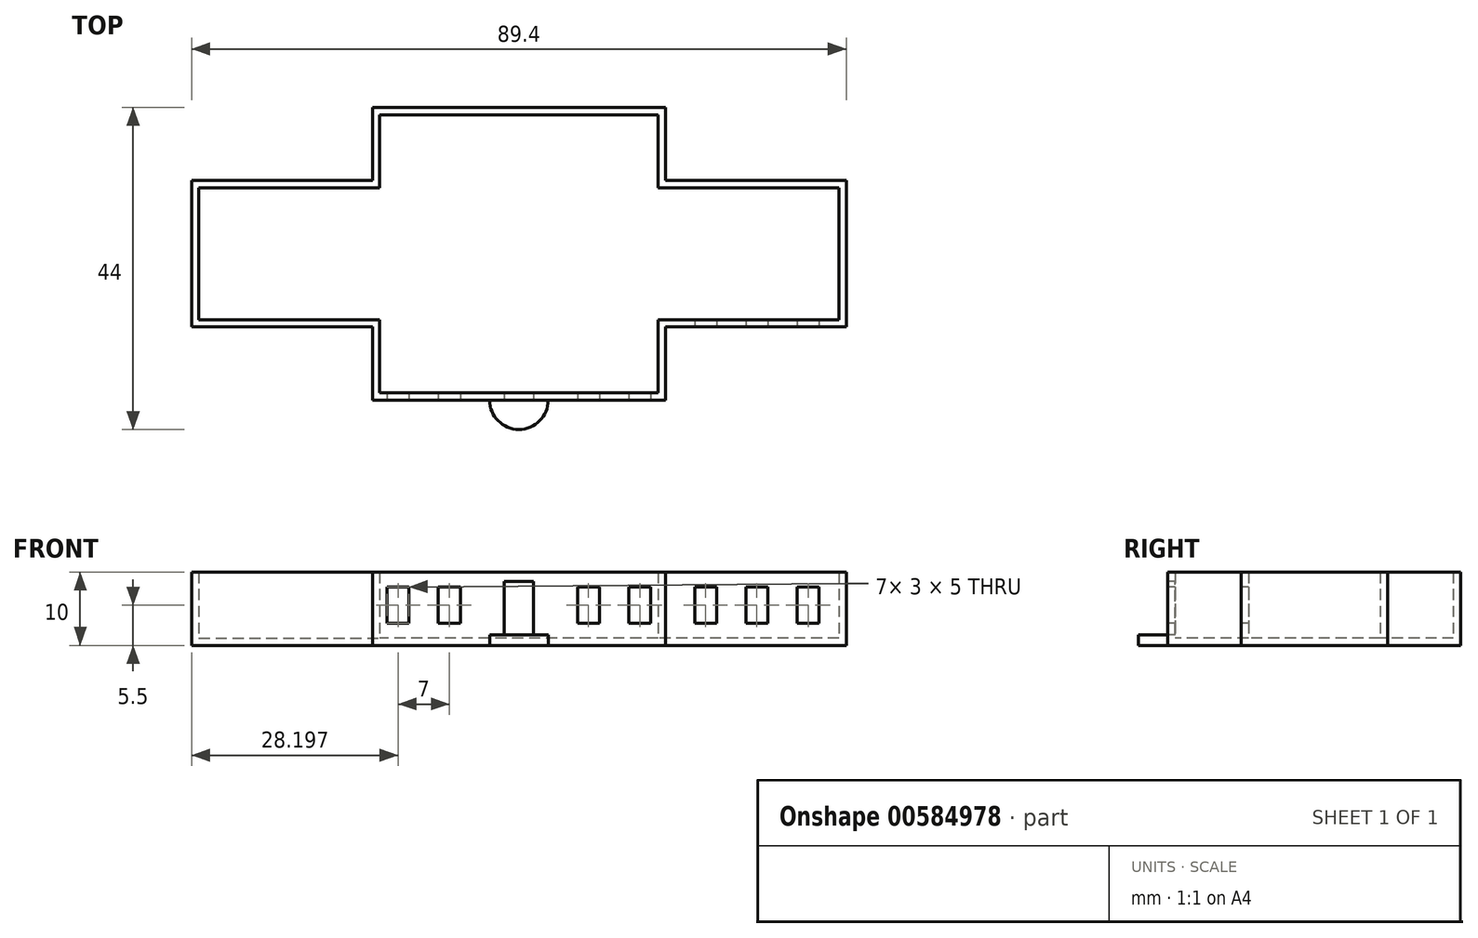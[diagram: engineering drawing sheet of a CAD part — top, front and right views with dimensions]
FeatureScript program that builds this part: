
annotation { "Feature Type Name" : "Feature", "Feature Type Description" : "" }
export const myFeature = defineFeature(function(context is Context, id is Id, definition is map)
    precondition{}
    {
        {
            var Q0;
            Q0=qCreatedBy(makeId("Top.planeOp"),FACE);
            var sketch = newSketch(context, id + "F0", { "sketchPlane" : qUnion([Q0])});
            skLineSegment(sketch, "E0", {"start": v(-44.66, 21.95) * mm, "end": v(-44.66, 31.95) * mm});
            skLineSegment(sketch, "E1", {"start": v(-44.66, 31.95) * mm, "end": v(-4.66, 31.95) * mm});
            skLineSegment(sketch, "E2", {"start": v(-4.66, 31.95) * mm, "end": v(-4.66, 21.95) * mm});
            skLineSegment(sketch, "E3", {"start": v(-4.66, 21.95) * mm, "end": v(20.04, 21.95) * mm});
            skLineSegment(sketch, "E4", {"start": v(20.04, 21.95) * mm, "end": v(20.04, 1.95) * mm});
            skLineSegment(sketch, "E5", {"start": v(20.04, 1.95) * mm, "end": v(-4.66, 1.95) * mm});
            skLineSegment(sketch, "E6", {"start": v(-4.66, 1.95) * mm, "end": v(-4.66, -8.05) * mm});
            skLineSegment(sketch, "E7", {"start": v(-4.66, -8.05) * mm, "end": v(-44.66, -8.05) * mm});
            skLineSegment(sketch, "E8", {"start": v(-44.66, -8.05) * mm, "end": v(-44.66, 1.95) * mm});
            skLineSegment(sketch, "E9", {"start": v(-44.66, 1.95) * mm, "end": v(-69.36, 1.95) * mm});
            skLineSegment(sketch, "E10", {"start": v(-69.36, 1.95) * mm, "end": v(-69.36, 21.95) * mm});
            skLineSegment(sketch, "E11", {"start": v(-69.36, 21.95) * mm, "end": v(-44.66, 21.95) * mm});
            skPoint(sketch, "E12", {"position": v(-24.66, -8.05) * mm});
            skCircle(sketch, "E13", {"center": v(-24.66, -8.05) * mm, "radius": 4 * mm});
            skPoint(sketch, "E14", {"position": v(-28.66, -8.05) * mm});
            skPoint(sketch, "E15", {"position": v(-20.66, -8.05) * mm});
            skSolve(sketch);
        }
        {
            var Q0;
            Q0=makeQuery(id+"F0.imprint","IMPRINT",FACE,{"disambiguationData":[TD([[makeQuery(id+"F0.imprint","IMPRINT",EDGE,{"derivedFrom":sQuery(id+"F0.wireOp",EDGE,"E0")}),-1.0]])]});
            var Q1;
            {var subQ0=sQuery(id+"F0.wireOp",EDGE,"E13");var subQ1=sQuery(id+"F0.wireOp",EDGE,"E7");var subQ2=makeQuery(id+"F0.imprint","INTERSECT",VERTEX,{"disambiguationData":[OD(0.0)],"derivedFrom":[subQ1,subQ0]});Q1=makeQuery(id+"F0.imprint","IMPRINT",FACE,{"disambiguationData":[TD([[makeQuery(id+"F0.imprint","IMPRINT",EDGE,{"disambiguationData":[TD([[subQ2,-1.0]])],"derivedFrom":subQ1}),-1.0]])]});}
            extrude(context, id + "F1", {"entities" : qUnion([Q0, Q1]), "depth" : 10 * mm, "offsetDistance" : 25 * mm});
        }
        {
            var Q0;
            Q0=makeQuery(id+"F1.opExtrude","CAP_FACE",FACE,{"disambiguationData":[OSD([sQuery(id+"F0.wireOp",EDGE,"E0"),sQuery(id+"F0.wireOp",EDGE,"E1"),sQuery(id+"F0.wireOp",EDGE,"E2"),sQuery(id+"F0.wireOp",EDGE,"E3"),sQuery(id+"F0.wireOp",EDGE,"E4"),sQuery(id+"F0.wireOp",EDGE,"E5"),sQuery(id+"F0.wireOp",EDGE,"E6"),sQuery(id+"F0.wireOp",EDGE,"E7"),sQuery(id+"F0.wireOp",EDGE,"E8"),sQuery(id+"F0.wireOp",EDGE,"E9"),sQuery(id+"F0.wireOp",EDGE,"E10"),sQuery(id+"F0.wireOp",EDGE,"E11")])],"isStart":false});
            shell(context, id + "F2", {"entities" : qUnion([Q0]), "thickness" : 1 * mm});
        }
        {
            var Q0;
            {var subQ0=sQuery(id+"F0.wireOp",EDGE,"E13");var subQ1=sQuery(id+"F0.wireOp",EDGE,"E7");var subQ2=makeQuery(id+"F0.imprint","INTERSECT",VERTEX,{"disambiguationData":[OD(0.0)],"derivedFrom":[subQ1,subQ0]});Q0=makeQuery(id+"F0.imprint","IMPRINT",FACE,{"disambiguationData":[TD([[makeQuery(id+"F0.imprint","IMPRINT",EDGE,{"disambiguationData":[TD([[subQ2,-1.0]])],"derivedFrom":subQ1}),1.0]])]});}
            extrude(context, id + "F3", {"entities" : qUnion([Q0]), "operationType" : NewBodyOperationType.ADD, "depth" : 1.4 * mm, "offsetDistance" : 25 * mm});
        }
        {
            var Q0;
            Q0=makeQuery(id+"F1.opExtrude","SWEPT_FACE",FACE,{"disambiguationData":[OSD([sQuery(id+"F0.wireOp",EDGE,"E7")])]});
            var sketch = newSketch(context, id + "F4", { "sketchPlane" : qUnion([Q0])});
            skLineSegment(sketch, "E16", {"start": v(-72.02, 8) * mm, "end": v(13.63, 8) * mm, "construction": true});
            skLineSegment(sketch, "E17.bottom", {"start": v(-42.66, 8) * mm, "end": v(-39.66, 8) * mm});
            skLineSegment(sketch, "E17.top", {"start": v(-42.66, 3) * mm, "end": v(-39.66, 3) * mm});
            skLineSegment(sketch, "E17.left", {"start": v(-42.66, 8) * mm, "end": v(-42.66, 3) * mm});
            skLineSegment(sketch, "E17.right", {"start": v(-39.66, 8) * mm, "end": v(-39.66, 3) * mm});
            skLineSegment(sketch, "E18.bottom", {"start": v(-35.66, 8) * mm, "end": v(-32.66, 8) * mm});
            skLineSegment(sketch, "E18.top", {"start": v(-35.66, 3) * mm, "end": v(-32.66, 3) * mm});
            skLineSegment(sketch, "E18.left", {"start": v(-35.66, 8) * mm, "end": v(-35.66, 3) * mm});
            skLineSegment(sketch, "E18.right", {"start": v(-32.66, 8) * mm, "end": v(-32.66, 3) * mm});
            skLineSegment(sketch, "E19.bottom", {"start": v(-16.66, 8) * mm, "end": v(-13.66, 8) * mm});
            skLineSegment(sketch, "E19.top", {"start": v(-16.66, 3) * mm, "end": v(-13.66, 3) * mm});
            skLineSegment(sketch, "E19.left", {"start": v(-16.66, 8) * mm, "end": v(-16.66, 3) * mm});
            skLineSegment(sketch, "E19.right", {"start": v(-13.66, 8) * mm, "end": v(-13.66, 3) * mm});
            skLineSegment(sketch, "E20.bottom", {"start": v(-9.66, 8) * mm, "end": v(-6.66, 8) * mm});
            skLineSegment(sketch, "E20.top", {"start": v(-9.66, 3) * mm, "end": v(-6.66, 3) * mm});
            skLineSegment(sketch, "E20.left", {"start": v(-9.66, 8) * mm, "end": v(-9.66, 3) * mm});
            skLineSegment(sketch, "E20.right", {"start": v(-6.66, 8) * mm, "end": v(-6.66, 3) * mm});
            skLineSegment(sketch, "E21.bottom", {"start": v(-22.66, 1.4) * mm, "end": v(-26.65, 1.4) * mm});
            skLineSegment(sketch, "E21.top", {"start": v(-22.66, 8.73) * mm, "end": v(-26.65, 8.73) * mm});
            skLineSegment(sketch, "E21.left", {"start": v(-22.66, 1.4) * mm, "end": v(-22.66, 8.73) * mm});
            skLineSegment(sketch, "E21.right", {"start": v(-26.65, 1.4) * mm, "end": v(-26.65, 8.73) * mm});
            skLineSegment(sketch, "E22.bottom", {"start": v(-0.66, 8) * mm, "end": v(2.34, 8) * mm});
            skLineSegment(sketch, "E22.top", {"start": v(-0.66, 3) * mm, "end": v(2.34, 3) * mm});
            skLineSegment(sketch, "E22.left", {"start": v(-0.66, 8) * mm, "end": v(-0.66, 3) * mm});
            skLineSegment(sketch, "E22.right", {"start": v(2.34, 8) * mm, "end": v(2.34, 3) * mm});
            skLineSegment(sketch, "E23.bottom", {"start": v(6.34, 8) * mm, "end": v(9.34, 8) * mm});
            skLineSegment(sketch, "E23.top", {"start": v(6.34, 3) * mm, "end": v(9.34, 3) * mm});
            skLineSegment(sketch, "E23.left", {"start": v(6.34, 8) * mm, "end": v(6.34, 3) * mm});
            skLineSegment(sketch, "E23.right", {"start": v(9.34, 8) * mm, "end": v(9.34, 3) * mm});
            skLineSegment(sketch, "E24.bottom", {"start": v(13.34, 8) * mm, "end": v(16.34, 8) * mm});
            skLineSegment(sketch, "E24.top", {"start": v(13.34, 3) * mm, "end": v(16.34, 3) * mm});
            skLineSegment(sketch, "E24.left", {"start": v(13.34, 8) * mm, "end": v(13.34, 3) * mm});
            skLineSegment(sketch, "E24.right", {"start": v(16.34, 8) * mm, "end": v(16.34, 3) * mm});
            skSolve(sketch);
        }
        {
            var Q0;
            Q0=makeQuery(id+"F4.imprint","IMPRINT",FACE,{"disambiguationData":[TD([[makeQuery(id+"F4.imprint","IMPRINT",EDGE,{"derivedFrom":sQuery(id+"F4.wireOp",EDGE,"E17.bottom")}),-1.0]])]});
            var Q1;
            Q1=makeQuery(id+"F4.imprint","IMPRINT",FACE,{"disambiguationData":[TD([[makeQuery(id+"F4.imprint","IMPRINT",EDGE,{"derivedFrom":sQuery(id+"F4.wireOp",EDGE,"E18.bottom")}),-1.0]])]});
            var Q2;
            Q2=makeQuery(id+"F4.imprint","IMPRINT",FACE,{"disambiguationData":[TD([[makeQuery(id+"F4.imprint","IMPRINT",EDGE,{"derivedFrom":sQuery(id+"F4.wireOp",EDGE,"E19.bottom")}),-1.0]])]});
            var Q3;
            Q3=makeQuery(id+"F4.imprint","IMPRINT",FACE,{"disambiguationData":[TD([[makeQuery(id+"F4.imprint","IMPRINT",EDGE,{"derivedFrom":sQuery(id+"F4.wireOp",EDGE,"E20.bottom")}),-1.0]])]});
            var Q4;
            Q4=makeQuery(id+"F4.imprint","IMPRINT",FACE,{"disambiguationData":[TD([[makeQuery(id+"F4.imprint","IMPRINT",EDGE,{"derivedFrom":sQuery(id+"F4.wireOp",EDGE,"E22.bottom")}),-1.0]])]});
            var Q5;
            Q5=makeQuery(id+"F4.imprint","IMPRINT",FACE,{"disambiguationData":[TD([[makeQuery(id+"F4.imprint","IMPRINT",EDGE,{"derivedFrom":sQuery(id+"F4.wireOp",EDGE,"E23.bottom")}),-1.0]])]});
            var Q6;
            Q6=makeQuery(id+"F4.imprint","IMPRINT",FACE,{"disambiguationData":[TD([[makeQuery(id+"F4.imprint","IMPRINT",EDGE,{"derivedFrom":sQuery(id+"F4.wireOp",EDGE,"E24.bottom")}),-1.0]])]});
            var Q7;
            Q7=makeQuery(id+"F4.imprint","IMPRINT",FACE,{"disambiguationData":[TD([[makeQuery(id+"F4.imprint","IMPRINT",EDGE,{"derivedFrom":sQuery(id+"F4.wireOp",EDGE,"E21.bottom")}),-1.0]])]});
            extrude(context, id + "F5", {"entities" : qUnion([Q0, Q1, Q2, Q3, Q4, Q5, Q6, Q7]), "operationType" : NewBodyOperationType.REMOVE, "oppositeDirection" : true, "depth" : 12 * mm, "offsetDistance" : 25 * mm});
        }
    });
